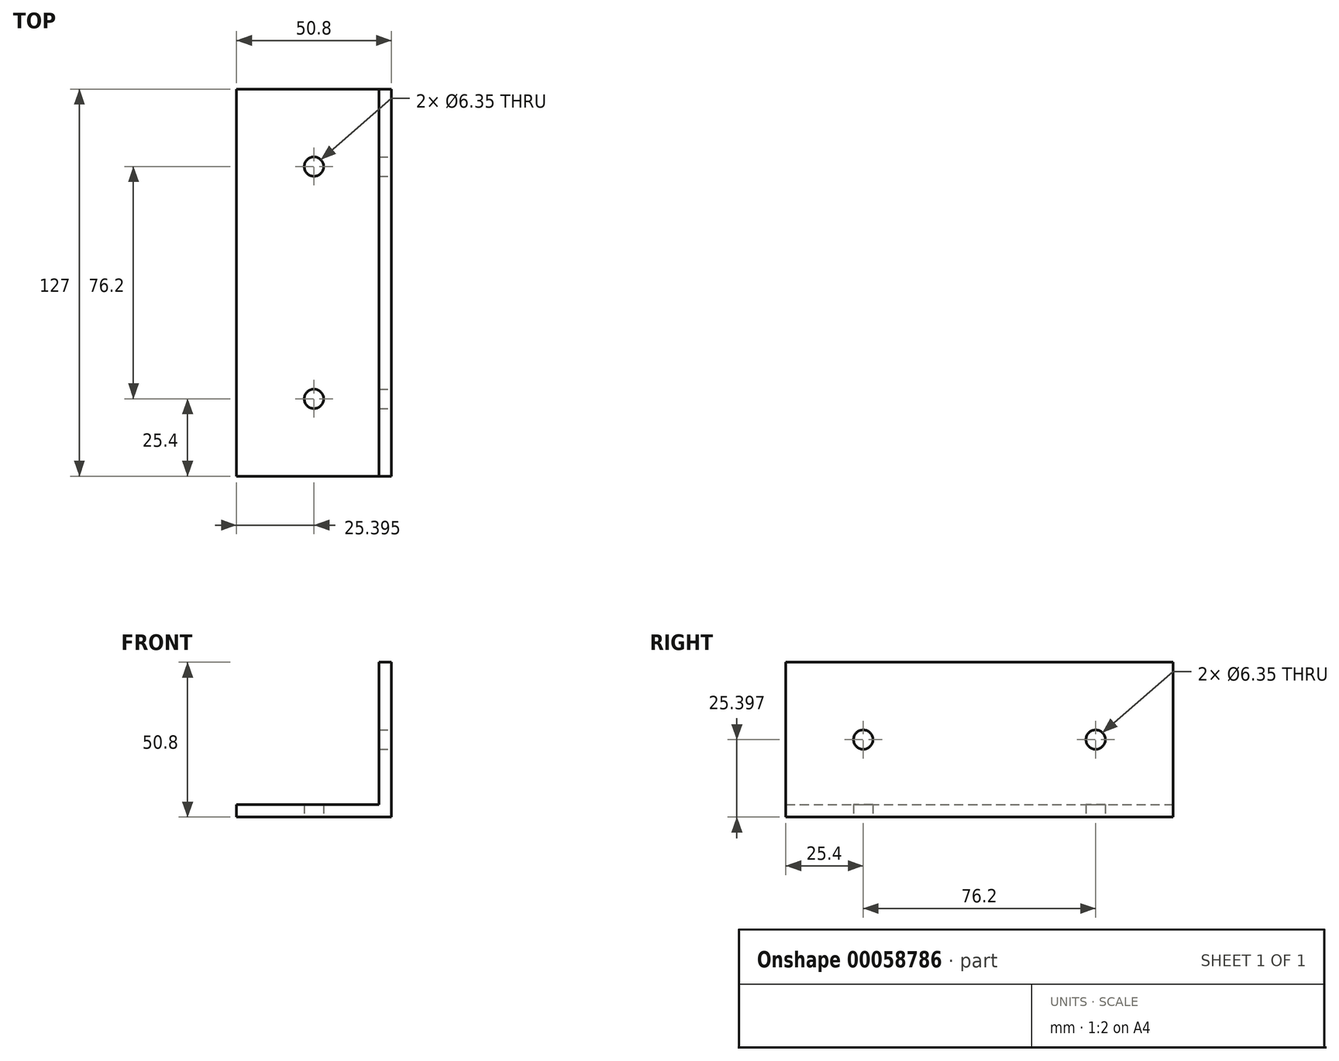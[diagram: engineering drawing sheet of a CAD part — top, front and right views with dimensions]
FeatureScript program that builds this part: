
annotation { "Feature Type Name" : "Feature", "Feature Type Description" : "" }
export const myFeature = defineFeature(function(context is Context, id is Id, definition is map)
    precondition{}
    {
        {
            var Q0;
            Q0=qCreatedBy(makeId("Front.planeOp"),FACE);
            var sketch = newSketch(context, id + "F0", { "sketchPlane" : qUnion([Q0])});
            skLineSegment(sketch, "E0.bottom", {"start": v(-66.14, 13.29) * mm, "end": v(-62.01, 13.29) * mm});
            skLineSegment(sketch, "E0.top", {"start": v(-66.14, -37.51) * mm, "end": v(-62.01, -37.51) * mm});
            skLineSegment(sketch, "E0.left", {"start": v(-66.14, 13.29) * mm, "end": v(-66.14, -37.51) * mm});
            skLineSegment(sketch, "E0.right", {"start": v(-62.01, 13.29) * mm, "end": v(-62.01, -37.51) * mm});
            skLineSegment(sketch, "E1.bottom", {"start": v(-62.01, -37.51) * mm, "end": v(-112.81, -37.51) * mm});
            skLineSegment(sketch, "E1.top", {"start": v(-62.01, -33.39) * mm, "end": v(-112.81, -33.39) * mm});
            skLineSegment(sketch, "E1.left", {"start": v(-62.01, -37.51) * mm, "end": v(-62.01, -33.39) * mm});
            skLineSegment(sketch, "E1.right", {"start": v(-112.81, -37.51) * mm, "end": v(-112.81, -33.39) * mm});
            skSolve(sketch);
        }
        {
            var Q0;
            Q0 = qSketchRegion(id + "F0", true);
            extrude(context, id + "F1", {"entities" : qUnion([Q0]), "depth" : 127 * mm});
        }
        {
            var Q0;
            Q0=makeQuery(id+"F1.opExtrude","SWEPT_FACE",FACE,{"disambiguationData":[OSD([sQuery(id+"F0.wireOp",EDGE,"E0.right"),sQuery(id+"F0.wireOp",EDGE,"E1.left")])]});
            var sketch = newSketch(context, id + "F2", { "sketchPlane" : qUnion([Q0])});
            skCircle(sketch, "E2", {"center": v(-25.4, -12.11) * mm, "radius": 3.18 * mm});
            skLineSegment(sketch, "E3", {"start": v(-63.5, 13.29) * mm, "end": v(-63.5, -37.51) * mm, "construction": true});
            skCircle(sketch, "E4.MirrorC", {"center": v(-101.6, -12.11) * mm, "radius": 3.18 * mm});
            skSolve(sketch);
        }
        {
            var Q0;
            Q0=makeQuery(id+"F1.opExtrude","SWEPT_FACE",FACE,{"disambiguationData":[OSD([sQuery(id+"F0.wireOp",EDGE,"E1.bottom")])]});
            var sketch = newSketch(context, id + "F3", { "sketchPlane" : qUnion([Q0])});
            skCircle(sketch, "E5", {"center": v(-87.41, 25.4) * mm, "radius": 3.18 * mm});
            skLineSegment(sketch, "E6", {"start": v(-62.01, 63.5) * mm, "end": v(-112.81, 63.5) * mm, "construction": true});
            skCircle(sketch, "E7.MirrorC", {"center": v(-87.41, 101.6) * mm, "radius": 3.18 * mm});
            skSolve(sketch);
        }
        {
            var Q0;
            Q0=sQuery(id+"F2.wireOp",VERTEX,"E4.MirrorC.center");
            var Q1;
            Q1=makeQuery(id+"F1.opExtrude","SWEPT_BODY",BODY,{"disambiguationData":[OSD([sQuery(id+"F0.wireOp",EDGE,"E0.bottom"),sQuery(id+"F0.wireOp",EDGE,"E0.left"),sQuery(id+"F0.wireOp",EDGE,"E0.right"),sQuery(id+"F0.wireOp",EDGE,"E1.bottom"),sQuery(id+"F0.wireOp",EDGE,"E1.top"),sQuery(id+"F0.wireOp",EDGE,"E1.left"),sQuery(id+"F0.wireOp",EDGE,"E1.right")])]});
            hole(context, id + "F4", {"style" : HoleStyle.SIMPLE, "holeDiameter" : 6.35 * mm, "endStyle" : HoleEndStyle.THROUGH, "locations" : qUnion([Q0]), "scope" : qUnion([Q1])});
        }
        {
            var Q0;
            Q0=sQuery(id+"F3.wireOp",VERTEX,"E7.MirrorC.center");
            var Q1;
            Q1=makeQuery(id+"F1.opExtrude","SWEPT_BODY",BODY,{"disambiguationData":[OSD([sQuery(id+"F0.wireOp",EDGE,"E0.bottom"),sQuery(id+"F0.wireOp",EDGE,"E0.left"),sQuery(id+"F0.wireOp",EDGE,"E0.right"),sQuery(id+"F0.wireOp",EDGE,"E1.bottom"),sQuery(id+"F0.wireOp",EDGE,"E1.top"),sQuery(id+"F0.wireOp",EDGE,"E1.left"),sQuery(id+"F0.wireOp",EDGE,"E1.right")])]});
            hole(context, id + "F5", {"style" : HoleStyle.SIMPLE, "holeDiameter" : 6.35 * mm, "endStyle" : HoleEndStyle.THROUGH, "locations" : qUnion([Q0]), "scope" : qUnion([Q1])});
        }
        {
            var Q0;
            Q0=sQuery(id+"F2.wireOp",VERTEX,"E2.center");
            var Q1;
            Q1=makeQuery(id+"F1.opExtrude","SWEPT_BODY",BODY,{"disambiguationData":[OSD([sQuery(id+"F0.wireOp",EDGE,"E0.bottom"),sQuery(id+"F0.wireOp",EDGE,"E0.left"),sQuery(id+"F0.wireOp",EDGE,"E0.right"),sQuery(id+"F0.wireOp",EDGE,"E1.bottom"),sQuery(id+"F0.wireOp",EDGE,"E1.top"),sQuery(id+"F0.wireOp",EDGE,"E1.left"),sQuery(id+"F0.wireOp",EDGE,"E1.right")])]});
            hole(context, id + "F6", {"style" : HoleStyle.SIMPLE, "holeDiameter" : 6.35 * mm, "endStyle" : HoleEndStyle.THROUGH, "locations" : qUnion([Q0]), "scope" : qUnion([Q1])});
        }
        {
            var Q0;
            Q0=sQuery(id+"F3.wireOp",VERTEX,"E5.center");
            var Q1;
            Q1=makeQuery(id+"F1.opExtrude","SWEPT_BODY",BODY,{"disambiguationData":[OSD([sQuery(id+"F0.wireOp",EDGE,"E0.bottom"),sQuery(id+"F0.wireOp",EDGE,"E0.left"),sQuery(id+"F0.wireOp",EDGE,"E0.right"),sQuery(id+"F0.wireOp",EDGE,"E1.bottom"),sQuery(id+"F0.wireOp",EDGE,"E1.top"),sQuery(id+"F0.wireOp",EDGE,"E1.left"),sQuery(id+"F0.wireOp",EDGE,"E1.right")])]});
            hole(context, id + "F7", {"style" : HoleStyle.SIMPLE, "holeDiameter" : 6.35 * mm, "endStyle" : HoleEndStyle.THROUGH, "locations" : qUnion([Q0]), "scope" : qUnion([Q1])});
        }
    });
